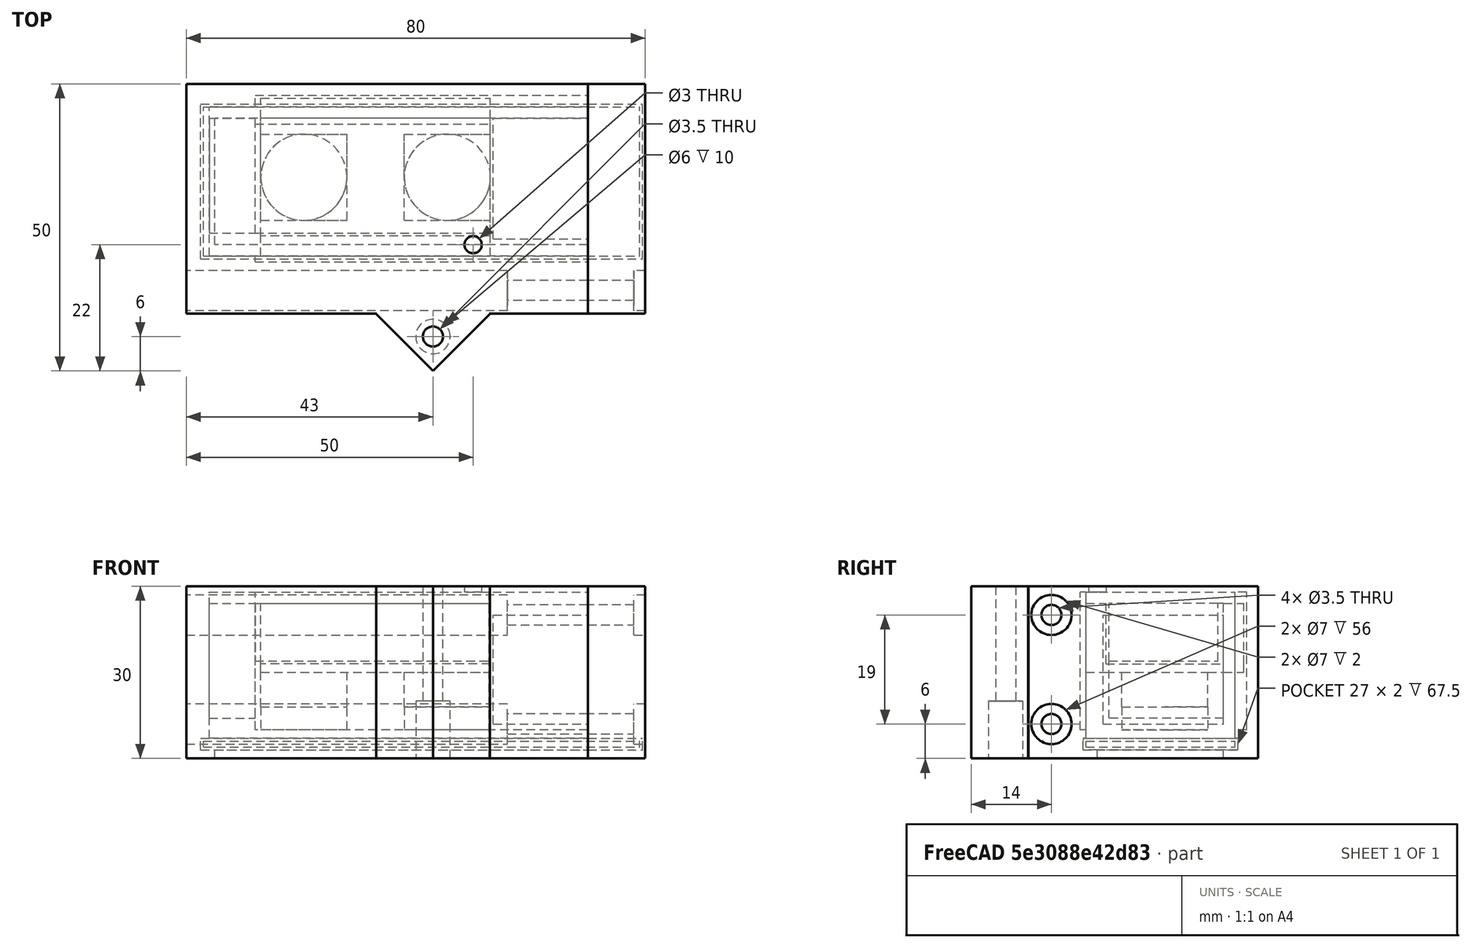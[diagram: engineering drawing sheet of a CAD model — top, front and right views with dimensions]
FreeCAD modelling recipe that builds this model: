
FCSTD DOCUMENT  (FreeCAD 0.21R0.20.1)
Label: ESP32CamMount
License: All rights reserved
LicenseURL: https://en.wikipedia.org/wiki/All_rights_reserved
objects: Part::Box×17, Part::Cylinder×12, Part::Cut×11, Part::MultiFuse×9
note: 49 computed .brp shape members not serialized (recipe doc carries the construction recipe); baked Part::Feature solids carry a one-line shape summary decoded from their .brp

FEATURE [Part::Box] Box  label="MicroscopeSlide"
  AttacherType = Attacher::AttachEngine3D
  Height = 1
  Length = 76
  Placement = pos=(0,0,-13) rot=(0,0,1;0rad)
  Width = 26
FEATURE [Part::Box] Box001  label="Cube001"
  AttacherType = Attacher::AttachEngine3D
  Height = 1.5
  Length = 40
  Width = 27.5
FEATURE [Part::Box] Box002  label="Cube"
  AttacherType = Attacher::AttachEngine3D
  Height = 12
  Length = 40
  Width = 3.5
FEATURE [Part::Box] Box003  label="Cube002"
  AttacherType = Attacher::AttachEngine3D
  Height = 12
  Length = 40
  Placement = pos=(0,24,0) rot=(0,0,1;0rad)
  Width = 3.5
FEATURE [Part::Cylinder] Cylinder
  Angle = 360
  AttacherType = Attacher::AttachEngine3D
  FirstAngle = 0
  Height = 4
  Placement = pos=(7.5,13.75,-10) rot=(0,0,1;0rad)
  Radius = 7.5
  SecondAngle = 0
FEATURE [Part::Box] Box005  label="Cube004"
  AttacherType = Attacher::AttachEngine3D
  Height = 30
  Length = 70
  Placement = pos=(-3,-10,-15) rot=(0,0,1;0rad)
  Width = 40
FEATURE [Part::Box] Box006  label="WindowOpening"
  AttacherType = Attacher::AttachEngine3D
  Height = 10
  Length = 72
  Placement = pos=(2,2,-23) rot=(0,0,1;0rad)
  Width = 22
FEATURE [Part::Cut] Cut
  Base = -> Box005
  Tool = -> Box006
FEATURE [Part::Box] Box007  label="MicroscopeSlideMount"
  AttacherType = Attacher::AttachEngine3D
  Height = 2
  Length = 77
  Placement = pos=(-0.5,-0.5,-13.5) rot=(0,0,1;0rad)
  Width = 27
FEATURE [Part::Cut] Cut001
  Base = -> Cut
  Tool = -> Box007
FEATURE [Part::Box] Box004  label="Cube003"
  AttacherType = Attacher::AttachEngine3D
  Height = 6
  Length = 15
  Placement = pos=(0,6.25,-6) rot=(0,0,1;0rad)
  Width = 15
FEATURE [Part::MultiFuse] Fusion001
  Placement = pos=(25,0,0) rot=(0,0,1;0rad)
  Shapes = -> [Box004,Cylinder]
FEATURE [Part::MultiFuse] Fusion  label="ESP32CamTemplate"
  Placement = pos=(10,0,0) rot=(0,0,1;0rad)
  Shapes = -> [Cylinder,Box001,Box002,Box003,Box004,Fusion001]
FEATURE [Part::Box] Box008  label="Cube005"
  AttacherType = Attacher::AttachEngine3D
  Height = 24
  Length = 100
  Placement = pos=(9,-1,-10) rot=(0,0,1;0rad)
  Width = 29
FEATURE [Part::Cut] Cut002
  Base = -> Cut001
  Tool = -> Box008
FEATURE [Part::Box] Box009  label="Cube006"
  AttacherType = Attacher::AttachEngine3D
  Height = 26
  Length = 100
  Placement = pos=(1,0,-12) rot=(0,0,1;0rad)
  Width = 26
FEATURE [Part::Cut] Cut003
  Base = -> Cut002
  Tool = -> Box009
FEATURE [Part::Box] Box010  label="Cube007"
  AttacherType = Attacher::AttachEngine3D
  Height = 10
  Length = 50
  Placement = pos=(0,4,2) rot=(0,0,1;0rad)
  Width = 19
FEATURE [Part::Box] Box011  label="Cube008"
  AttacherType = Attacher::AttachEngine3D
  Height = 20
  Length = 9
  Placement = pos=(0,4,-8) rot=(0,0,1;0rad)
  Width = 20
FEATURE [Part::MultiFuse] Fusion002  label="HousingAWB"
  Shapes = -> [Cut003,Box010,Box011]
FEATURE [Part::Box] Box012  label="Cube009"
  AttacherType = Attacher::AttachEngine3D
  Height = 30
  Length = 10
  Placement = pos=(67,-10,-15) rot=(0,0,1;0rad)
  Width = 40
FEATURE [Part::Box] Box013  label="MicroscopeSlideMount001"
  AttacherType = Attacher::AttachEngine3D
  Height = 2
  Length = 77
  Placement = pos=(-0.5,-0.5,-13.5) rot=(0,0,1;0rad)
  Width = 27
FEATURE [Part::Cut] Cut004
  Base = -> Box012
  Tool = -> Box013
FEATURE [Part::Box] Box014  label="Cube010"
  AttacherType = Attacher::AttachEngine3D
  Height = 19
  Length = 25
  Placement = pos=(50.5,3,-9) rot=(0,0,1;0rad)
  Width = 21
FEATURE [Part::MultiFuse] Fusion003
  Shapes = -> [Box014,Cut004]
FEATURE [Part::Cylinder] Cylinder001
  Angle = 360
  AttacherType = Attacher::AttachEngine3D
  FirstAngle = 0
  Height = 100
  Placement = pos=(-10,-6,-9) rot=(0,1,0;1.5708rad)
  Radius = 1.75
  SecondAngle = 0
FEATURE [Part::Cylinder] Cylinder002
  Angle = 360
  AttacherType = Attacher::AttachEngine3D
  FirstAngle = 0
  Height = 100
  Placement = pos=(-10,-6,10) rot=(0,1,0;1.5708rad)
  Radius = 1.75
  SecondAngle = 0
FEATURE [Part::Cylinder] Cylinder003
  Angle = 360
  AttacherType = Attacher::AttachEngine3D
  FirstAngle = 0
  Height = 100
  Placement = pos=(-10,-6,-9) rot=(0,1,0;1.5708rad)
  Radius = 1.75
  SecondAngle = 0
FEATURE [Part::Cylinder] Cylinder004
  Angle = 360
  AttacherType = Attacher::AttachEngine3D
  FirstAngle = 0
  Height = 100
  Placement = pos=(-10,-6,10) rot=(0,1,0;1.5708rad)
  Radius = 1.75
  SecondAngle = 0
FEATURE [Part::MultiFuse] Fusion004
  Shapes = -> [Cylinder001,Cylinder002]
FEATURE [Part::Cut] Cut005
  Base = -> Fusion002
  Tool = -> Fusion004
FEATURE [Part::Cylinder] Cylinder005
  Angle = 360
  AttacherType = Attacher::AttachEngine3D
  FirstAngle = 0
  Height = 100
  Placement = pos=(-47,-6,10) rot=(0,1,0;1.5708rad)
  Radius = 3.5
  SecondAngle = 0
FEATURE [Part::Cylinder] Cylinder006
  Angle = 360
  AttacherType = Attacher::AttachEngine3D
  FirstAngle = 0
  Height = 100
  Placement = pos=(-47,-6,-9) rot=(0,1,0;1.5708rad)
  Radius = 3.5
  SecondAngle = 0
FEATURE [Part::MultiFuse] Fusion005
  Shapes = -> [Cylinder005,Cylinder006]
FEATURE [Part::Cut] Cut006  label="HousingA_NoMount"
  Base = -> Cut005
  Tool = -> Fusion005
FEATURE [Part::Cylinder] Cylinder007
  Angle = 360
  AttacherType = Attacher::AttachEngine3D
  FirstAngle = 0
  Height = 2
  Placement = pos=(75,-6,10) rot=(0,1,0;1.5708rad)
  Radius = 3.5
  SecondAngle = 0
FEATURE [Part::Cylinder] Cylinder008
  Angle = 360
  AttacherType = Attacher::AttachEngine3D
  FirstAngle = 0
  Height = 2
  Placement = pos=(75,-6,-9) rot=(0,1,0;1.5708rad)
  Radius = 3.5
  SecondAngle = 0
FEATURE [Part::MultiFuse] Fusion006
  Shapes = -> [Cylinder008,Cylinder007,Cylinder004,Cylinder003]
FEATURE [Part::Cut] Cut007  label="HousingB"
  Base = -> Fusion003
  Tool = -> Fusion006
FEATURE [Part::Cylinder] Cylinder009
  Angle = 360
  AttacherType = Attacher::AttachEngine3D
  FirstAngle = 0
  Height = 10
  Placement = pos=(47,2,10) rot=(0,0,1;0rad)
  Radius = 1.5
  SecondAngle = 0
FEATURE [Part::Cut] Cut008
  Base = -> Cut006
  Tool = -> Cylinder009
FEATURE [Part::Box] Box015  label="Cube011"
  AttacherType = Attacher::AttachEngine3D
  Height = 30
  Length = 14
  Placement = pos=(0,-3,0) rot=(0,0,1;0.785398rad)
  Width = 14
FEATURE [Part::Box] Box016  label="Cube012"
  AttacherType = Attacher::AttachEngine3D
  Height = 30
  Length = 20
  Placement = pos=(-10,7,0) rot=(0,0,1;0rad)
  Width = 20
FEATURE [Part::Cylinder] Cylinder010
  Angle = 360
  AttacherType = Attacher::AttachEngine3D
  FirstAngle = 0
  Height = 30
  Placement = pos=(0,3,0) rot=(0,0,1;0rad)
  Radius = 1.75
  SecondAngle = 0
FEATURE [Part::Cylinder] Cylinder011
  Angle = 360
  AttacherType = Attacher::AttachEngine3D
  FirstAngle = 0
  Height = 10
  Placement = pos=(0,3,0) rot=(0,0,1;0rad)
  Radius = 3
  SecondAngle = 0
FEATURE [Part::MultiFuse] Fusion007
  Shapes = -> [Cylinder011,Cylinder010]
FEATURE [Part::Cut] Cut009
  Base = -> Box015
  Tool = -> Fusion007
FEATURE [Part::Cut] Cut010
  Base = -> Cut009
  Placement = pos=(40,-17,-15) rot=(0,0,1;0rad)
  Tool = -> Box016
FEATURE [Part::MultiFuse] Fusion008  label="HousingAWithMount"
  Shapes = -> [Cut008,Cut010]
